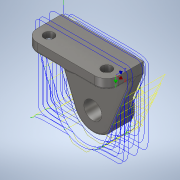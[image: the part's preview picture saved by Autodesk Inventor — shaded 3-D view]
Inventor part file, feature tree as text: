
AUTODESK INVENTOR PART (.ipt)
format: ipt  version: 2020 (Build 240168000, 168)  size: 421,888 bytes
history: native  units: mm
features: extrude x5, sketch x4, fillet x2, plane x1, rib x1
ambient origin geometry x8: Origin, YZ Plane, XZ Plane, XY Plane, X Axis, Y Axis, Z Axis, Center Point
bodies: Solid1 (feature_tree)
feature tree (13):
  extrude  "Extrusion1"  Depth=41.0mm
  sketch  "Sketch2"  dims[d2=18.0mm d3=22.0mm d4=0.0mm]
  extrude  "Extrusion2"  Depth=22.0mm TaperAngle=0.0deg
  extrude  "Extrusion3"  Depth=41.0mm
  plane  "Work Plane1"
  rib  "Rib1"
  sketch  "Sketch6"  dims[d7=10.0mm d8=10.0mm d9=0.0mm d10=27.0mm d11=0.0mm d12=-41.0mm d17=1.0mm d18=10.0mm d19=0.0mm d20=0.0mm d21=1.0mm d22=1.0mm d23=10.0mm d24=22.0mm d25=22.0mm d26=10.0mm d27=12.0mm d28=12.0mm d29=12.0mm d30=12.0mm d31=27.0mm d32=0.0mm d33=4.0mm d34=0.0mm d35=12.0mm d37=2.0mm]
  extrude  "Extrusion4"  Depth=10.0mm TaperAngle=0.0deg
  extrude  "Extrusion5"  Depth=27.0mm TaperAngle=0.0deg
  fillet  "Fillet1"  [1 undecoded]
  fillet  "Fillet3"  Radius=1.0mm
  sketch  "Sketch1"  dims[d0=40.0mm d1=41.0mm]
  sketch  "Sketch5"  dims[d5=82.0mm d6=41.0mm]
note: 1 required parameter value undecoded (feature->parameter linkage not recoverable at this tier; creation-order binding heuristic only, values carry confidence <= 0.55)
